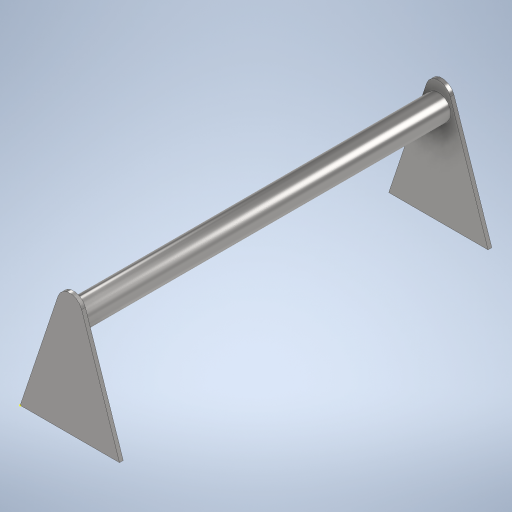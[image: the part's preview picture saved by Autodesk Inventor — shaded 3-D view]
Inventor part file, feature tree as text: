
AUTODESK INVENTOR PART (.ipt)
format: ipt  version: 2023 (Build 270158030, 158C)  size: 280,576 bytes
history: native  units: mm
features: sketch x3, extrude x2, fillet x2, mirror x1
ambient origin geometry x8: Origin, YZ Plane, XZ Plane, XY Plane, X Axis, Y Axis, Z Axis, Center Point
bodies: Solid1 (feature_tree)
feature tree (8):
  sketch  "Sketch1"  dims[d0=80.0mm d1=120.0mm d2=40.0mm]
  extrude  "Extrusion1"  Depth=80.0mm
  sketch  "Sketch3"  dims[d7=80.0mm d8=10.0mm d9=147.0mm d10=0.0mm d11=10.0mm]
  fillet  "Fillet1"  Radius=40.0mm
  extrude  "Extrusion2"  Depth=3.0mm
  mirror  "Mirror1"
  fillet  "Fillet2"  [1 undecoded]
  sketch  "Sketch2"  dims[d3=3.0mm d4=0.0mm d5=20.0mm d6=0.0mm]
note: 1 required parameter value undecoded (feature->parameter linkage not recoverable at this tier; creation-order binding heuristic only, values carry confidence <= 0.55)
